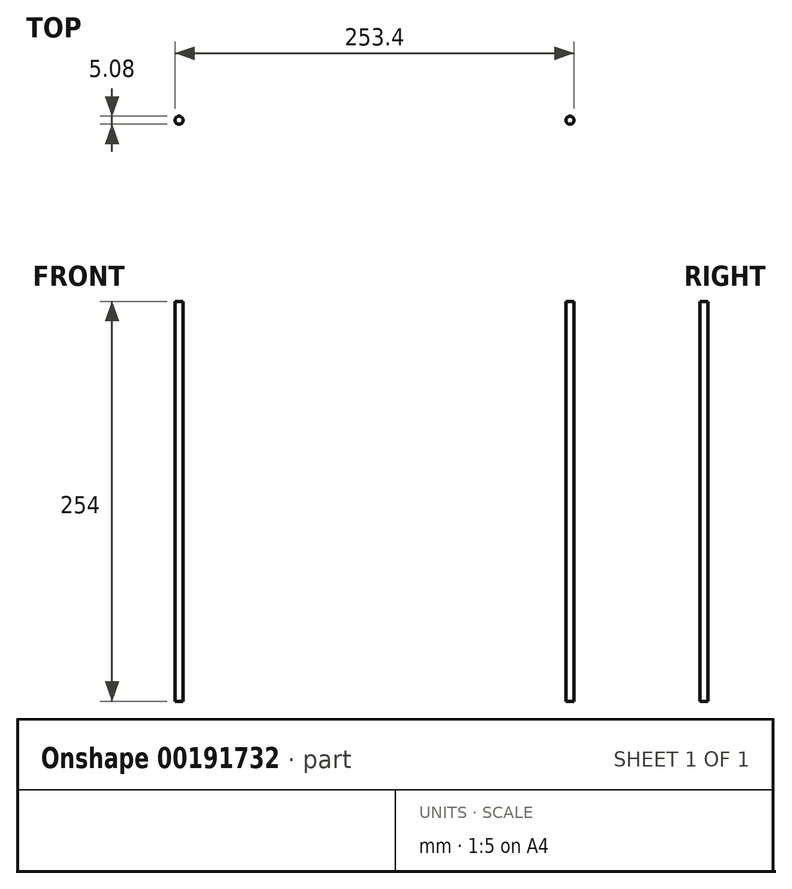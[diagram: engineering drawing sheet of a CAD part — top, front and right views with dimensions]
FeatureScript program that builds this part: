
annotation { "Feature Type Name" : "Feature", "Feature Type Description" : "" }
export const myFeature = defineFeature(function(context is Context, id is Id, definition is map)
    precondition{}
    {
        {
            var Q0;
            Q0=qCreatedBy(makeId("Front.planeOp"),FACE);
            var sketch = newSketch(context, id + "F0", { "sketchPlane" : qUnion([Q0])});
            skLineSegment(sketch, "E0", {"start": v(-124.16, 0) * mm, "end": v(-124.16, 254) * mm});
            skSolve(sketch);
        }
        {
            var Q0;
            Q0=qCreatedBy(makeId("Top.planeOp"),FACE);
            var sketch = newSketch(context, id + "F1", { "sketchPlane" : qUnion([Q0])});
            skCircle(sketch, "E1", {"center": v(-124.16, 0) * mm, "radius": 2.54 * mm});
            skSolve(sketch);
        }
        {
            var Q0;
            Q0=makeQuery(id+"F1.imprint","IMPRINT",FACE,{"disambiguationData":[TD([[makeQuery(id+"F1.imprint","IMPRINT",EDGE,{"derivedFrom":sQuery(id+"F1.wireOp",EDGE,"E1")}),1.0]])]});
            var Q1;
            Q1 = qConstructionFilter(qBodyType(qCreatedBy(id + "F0" ,EDGE), BodyType.WIRE), ConstructionObject.NO);
            sweep(context, id + "F2", {"profiles" : qUnion([Q0]), "path" : qUnion([Q1])});
        }
        {
            var Q0;
            Q0=makeQuery(id+"F2.opSweep","SWEPT_BODY",BODY,{"disambiguationData":[OSD([sQuery(id+"F0.wireOp",EDGE,"E0"),sQuery(id+"F1.wireOp",EDGE,"E1")])]});
            var Q1;
            Q1=qCreatedBy(makeId("Right.planeOp"),FACE);
            mirror(context, id + "F3", {"entities" : qUnion([Q0]), "mirrorPlane" : qUnion([Q1])});
        }
    });
